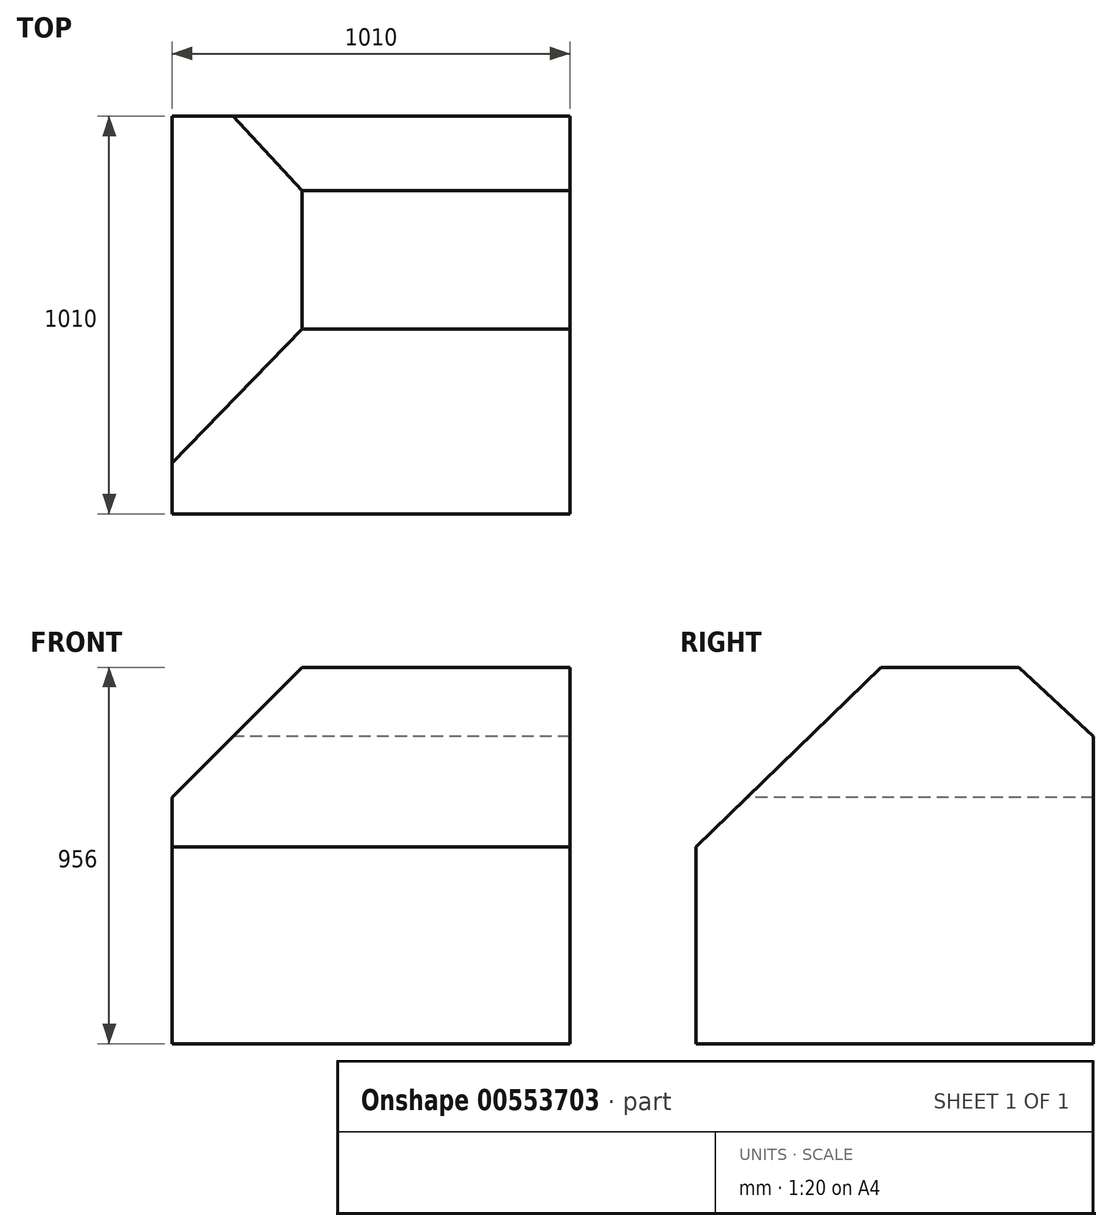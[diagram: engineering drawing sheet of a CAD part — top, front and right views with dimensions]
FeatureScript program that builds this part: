
annotation { "Feature Type Name" : "Feature", "Feature Type Description" : "" }
export const myFeature = defineFeature(function(context is Context, id is Id, definition is map)
    precondition{}
    {
        {
            var Q0;
            Q0=qCreatedBy(makeId("Top.planeOp"),FACE);
            var sketch = newSketch(context, id + "F0", { "sketchPlane" : qUnion([Q0])});
            skLineSegment(sketch, "E0.bottom", {"start": v(-505, 505) * mm, "end": v(505, 505) * mm});
            skLineSegment(sketch, "E0.top", {"start": v(-505, -505) * mm, "end": v(505, -505) * mm});
            skLineSegment(sketch, "E0.left", {"start": v(-505, 505) * mm, "end": v(-505, -505) * mm});
            skLineSegment(sketch, "E0.right", {"start": v(505, 505) * mm, "end": v(505, -505) * mm});
            skPoint(sketch, "E0.middle", {"position": v(0, 0) * mm});
            skSolve(sketch);
        }
        {
            var Q0;
            Q0=makeQuery(id+"F0.imprint","IMPRINT",FACE,{"disambiguationData":[TD([[makeQuery(id+"F0.imprint","IMPRINT",EDGE,{"derivedFrom":sQuery(id+"F0.wireOp",EDGE,"E0.bottom")}),-1.0]])]});
            extrude(context, id + "F1", {"entities" : qUnion([Q0]), "depth" : 956 * mm, "offsetDistance" : 25 * mm});
        }
        {
            var Q0;
            Q0=makeQuery(id+"F1.opExtrude","SWEPT_FACE",FACE,{"disambiguationData":[OSD([sQuery(id+"F0.wireOp",EDGE,"E0.left")])]});
            var sketch = newSketch(context, id + "F2", { "sketchPlane" : qUnion([Q0])});
            skLineSegment(sketch, "E1", {"start": v(-505, 781) * mm, "end": v(-316, 956) * mm});
            skLineSegment(sketch, "E2", {"start": v(505, 500) * mm, "end": v(35, 956) * mm});
            skLineSegment(sketch, "E3", {"start": v(505, 500) * mm, "end": v(505, 956) * mm});
            skLineSegment(sketch, "E4", {"start": v(505, 956) * mm, "end": v(35, 956) * mm});
            skLineSegment(sketch, "E5", {"start": v(-316, 956) * mm, "end": v(-505, 956) * mm});
            skLineSegment(sketch, "E6", {"start": v(-505, 956) * mm, "end": v(-505, 781) * mm});
            skSolve(sketch);
        }
        {
            var Q0;
            Q0=makeQuery(id+"F2.imprint","IMPRINT",FACE,{"disambiguationData":[TD([[makeQuery(id+"F2.imprint","IMPRINT",EDGE,{"derivedFrom":sQuery(id+"F2.wireOp",EDGE,"E1")}),1.0]])]});
            extrude(context, id + "F3", {"entities" : qUnion([Q0]), "operationType" : NewBodyOperationType.REMOVE, "oppositeDirection" : true, "depth" : 1010 * mm, "offsetDistance" : 25 * mm});
        }
        {
            var Q0;
            Q0=makeQuery(id+"F2.imprint","IMPRINT",FACE,{"disambiguationData":[TD([[makeQuery(id+"F2.imprint","IMPRINT",EDGE,{"derivedFrom":sQuery(id+"F2.wireOp",EDGE,"E2")}),-1.0]])]});
            extrude(context, id + "F4", {"entities" : qUnion([Q0]), "operationType" : NewBodyOperationType.REMOVE, "oppositeDirection" : true, "depth" : 1010 * mm, "offsetDistance" : 25 * mm});
        }
        {
            var Q0;
            Q0=makeQuery(id+"F1.opExtrude","SWEPT_FACE",FACE,{"disambiguationData":[OSD([sQuery(id+"F0.wireOp",EDGE,"E0.top")])]});
            var sketch = newSketch(context, id + "F5", { "sketchPlane" : qUnion([Q0])});
            skLineSegment(sketch, "E7.0", {"start": v(505, 956) * mm, "end": v(175, 956) * mm});
            skLineSegment(sketch, "E8", {"start": v(-175, 956) * mm, "end": v(-505, 956) * mm});
            skLineSegment(sketch, "E9", {"start": v(-505, 626) * mm, "end": v(-175, 956) * mm});
            skLineSegment(sketch, "E10", {"start": v(175, 956) * mm, "end": v(505, 956) * mm});
            skLineSegment(sketch, "E11", {"start": v(505, 626) * mm, "end": v(175, 956) * mm});
            skLineSegment(sketch, "E12", {"start": v(505, 956) * mm, "end": v(505, 626) * mm});
            skLineSegment(sketch, "E13", {"start": v(-505, 626) * mm, "end": v(-505, 956) * mm});
            skSolve(sketch);
        }
        {
            var Q0;
            Q0=makeQuery(id+"F5.imprint","IMPRINT",FACE,{"disambiguationData":[TD([[makeQuery(id+"F5.imprint","IMPRINT",EDGE,{"derivedFrom":sQuery(id+"F5.wireOp",EDGE,"E9")}),1.0]])]});
            var Q1;
            Q1=makeQuery(id+"F5.imprint","IMPRINT",FACE,{"disambiguationData":[TD([[makeQuery(id+"F5.imprint","IMPRINT",EDGE,{"derivedFrom":sQuery(id+"F5.wireOp",EDGE,"E10")}),-1.0]])]});
            extrude(context, id + "F6", {"entities" : qUnion([Q0, Q1]), "operationType" : NewBodyOperationType.REMOVE, "oppositeDirection" : true, "depth" : 1010 * mm, "offsetDistance" : 25 * mm});
        }
    });
